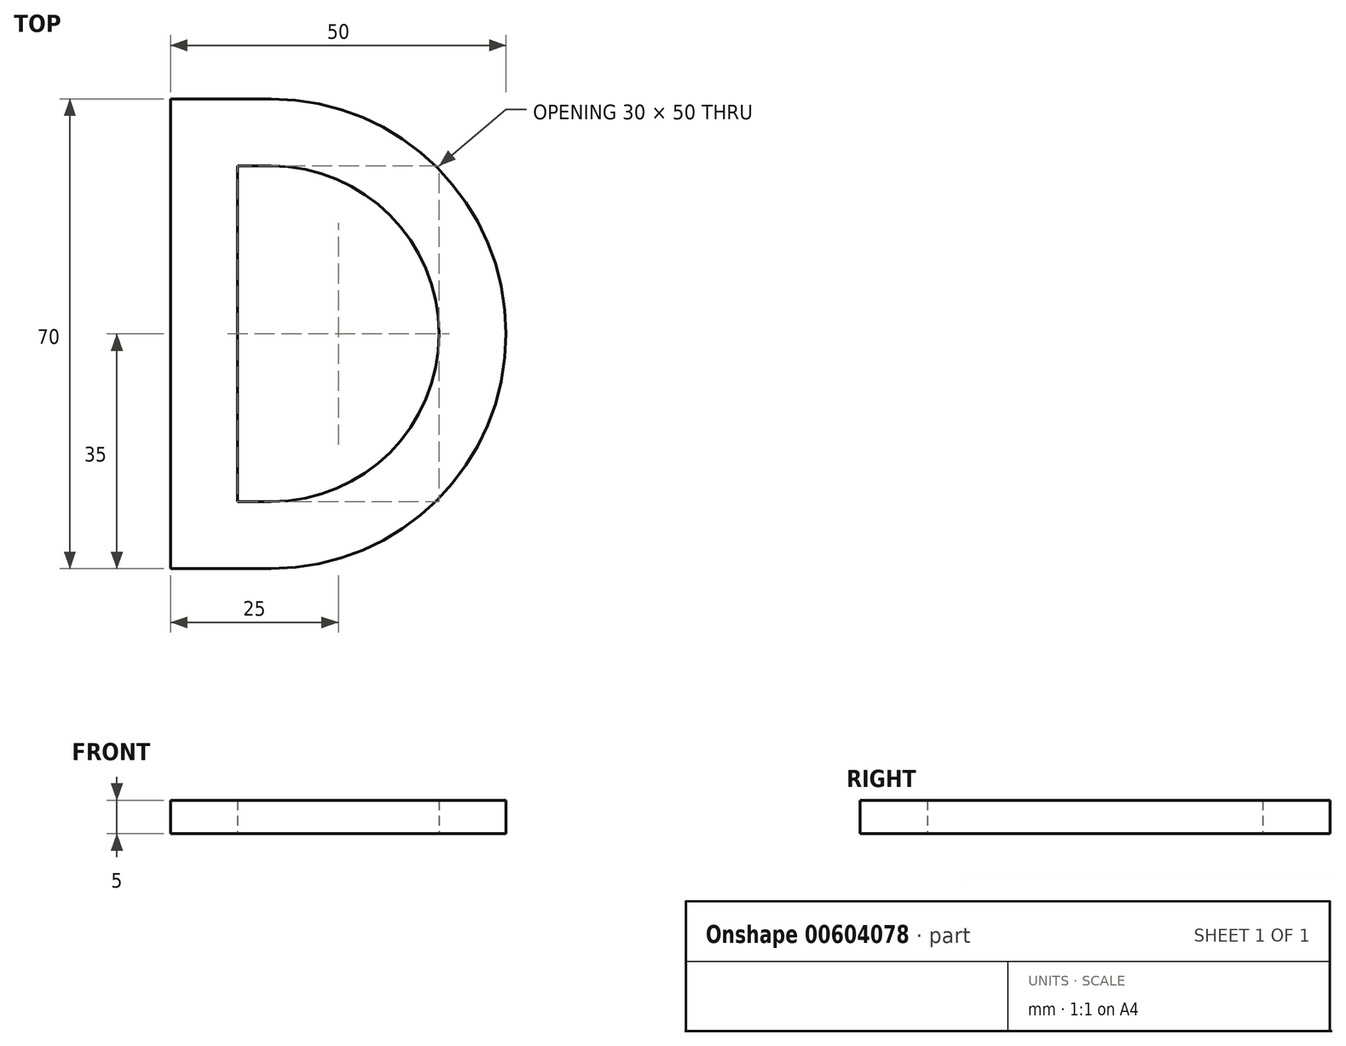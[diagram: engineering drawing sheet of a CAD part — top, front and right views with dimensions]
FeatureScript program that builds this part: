
annotation { "Feature Type Name" : "Feature", "Feature Type Description" : "" }
export const myFeature = defineFeature(function(context is Context, id is Id, definition is map)
    precondition{}
    {
        {
            var Q0;
            Q0=qCreatedBy(makeId("Top.planeOp"),FACE);
            var sketch = newSketch(context, id + "F0", { "sketchPlane" : qUnion([Q0])});
            skLineSegment(sketch, "E0", {"start": v(0, 0) * mm, "end": v(0, 70) * mm});
            skLineSegment(sketch, "E1", {"start": v(0, 70) * mm, "end": v(15, 70) * mm});
            skLineSegment(sketch, "E2", {"start": v(15, 60) * mm, "end": v(10, 60) * mm});
            skLineSegment(sketch, "E3", {"start": v(10, 60) * mm, "end": v(10, 10) * mm});
            skLineSegment(sketch, "E4", {"start": v(10, 10) * mm, "end": v(15, 10) * mm});
            skLineSegment(sketch, "E5", {"start": v(15, 0) * mm, "end": v(0, 0) * mm});
            skArc(sketch, "E6", {"start": v(15, 0) * mm, "mid": v(50, 35) * mm, "end": v(15, 70) * mm});
            skArc(sketch, "E7", {"start": v(15, 10) * mm, "mid": v(40, 35) * mm, "end": v(15, 60) * mm});
            skSolve(sketch);
        }
        {
            var Q0;
            Q0=makeQuery(id+"F0.imprint","IMPRINT",FACE,{"disambiguationData":[TD([[makeQuery(id+"F0.imprint","IMPRINT",EDGE,{"derivedFrom":sQuery(id+"F0.wireOp",EDGE,"E0")}),-1.0]])]});
            extrude(context, id + "F1", {"entities" : qUnion([Q0]), "depth" : 5 * mm, "offsetDistance" : 25.4 * mm});
        }
    });
